# Revit family: Block 600-1600
name_source: partatom
category: Оборудование
units: mm (PartAtom-declared; Revit-internal decimal feet)

## family parameters
Всегда вертикально = Да
Классификация = Нет
На основе рабочей плоскости = Нет
Общий = Нет
При загрузке вырезать с полостями = Нет
Размер круглого соединителя = Использовать диаметр
Тип детали = Нормальный
Точка расчета площади = Нет

## types (3) — shared parameters
ADSK_Единица измерения = шт.
ADSK_Завод-изготовитель = ООО «Турков»
ADSK_Количество фаз = 1
ADSK_Наименование = Канальный очиститель с высокой степенью фильтрации Block
ADSK_Напряжение = 220 В
ВВ_толщ = 45 мм
КА_y = 45 мм
КА_высота = 100 мм
КА_толщина = 50 мм
КА_ширина = 100 мм
Кол-во вентиляторов = 1
zero-valued in all types: ADSK_Масса

## per-type parameters (varying)
| type | A1 длина | ADSK_Номинальная мощность | ADSK_Свободный напор воздуха | ADSK_Ток | B1 глубина | C1 высота | ВВ_Dn | ВВ_У | СЗ | Угол УГО |
| Block 600 | 805 мм | 160 Вт | 0.0 Па | 1 А | 340 мм | 560 мм | 200 мм | 165 мм | 320 мм | 24.23° |
| Block 1100 | 1085 мм | 500 Вт | 140.0 Па | 2 А | 390 мм | 660 мм | 250 мм | 225 мм | 400 мм | 19.80° |
| Block 1600 | 1085 мм | 750 Вт | 522.0 Па | 3 А | 440 мм | 660 мм | 315 мм | 250 мм | 500 мм | 15.95° |

note: column(s) folded — value = type name in every type: ADSK_Марка

## geometry (parser evidence)
native form markers: Sweep x4
no freeform markers — native parametric forms only
